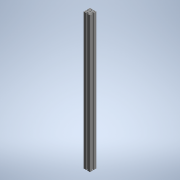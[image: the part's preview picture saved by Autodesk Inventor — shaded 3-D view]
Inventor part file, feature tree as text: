
AUTODESK INVENTOR PART (.ipt)
format: ipt  version: 2022 (Build 260153000, 153)  size: 225,280 bytes
history: native  units: mm (DEFAULTED — no unit token found)
features: other x21, sketch x2, extrude x1, hole x1
ambient origin geometry x8: Origin, YZ Plane, XZ Plane, XY Plane, X Axis, Y Axis, Z Axis, Center Point
bodies: Solid1 (feature_tree)
feature tree (25):
  extrude  "Extrusion1"  TaperAngle=0.0deg  [1 undecoded]
  hole  "Hole1"  [1 undecoded]
  other  "C1_XY"
  other  "C1_YZ"
  other  "C1_ZX"
  other  "C1_X"
  other  "C1_Y"
  other  "C1_Z"
  other  "C1_Center"
  other  "to_frame_cap1_XY"
  other  "to_frame_cap1_YZ"
  other  "to_frame_cap1_ZX"
  other  "to_frame_cap1_X"
  other  "to_frame_cap1_Y"
  other  "to_frame_cap1_Z"
  other  "to_frame_cap1_Center"
  other  "to_frame_cap2_XY"
  other  "to_frame_cap2_YZ"
  other  "to_frame_cap2_ZX"
  other  "to_frame_cap2_X"
  other  "to_frame_cap2_Y"
  other  "to_frame_cap2_Z"
  other  "to_frame_cap2_Center"
  sketch  "Sketch_60"  dims[d2=10.5mm d3=6.0mm d4=4.0mm d5=2.0mm d6=90.0deg d7=1000.0mm d8=0.0mm d9=0.0mm d10=0.0mm d11=0.0mm d12=152.4mm d13=0.872665mm d14=152.4mm d15=0.872665mm]
  sketch  "Sketch2"  dims[d0=1270.0mm d1=0.0mm]
note: 2 required parameter values undecoded (feature->parameter linkage not recoverable at this tier; creation-order binding heuristic only, values carry confidence <= 0.55)
